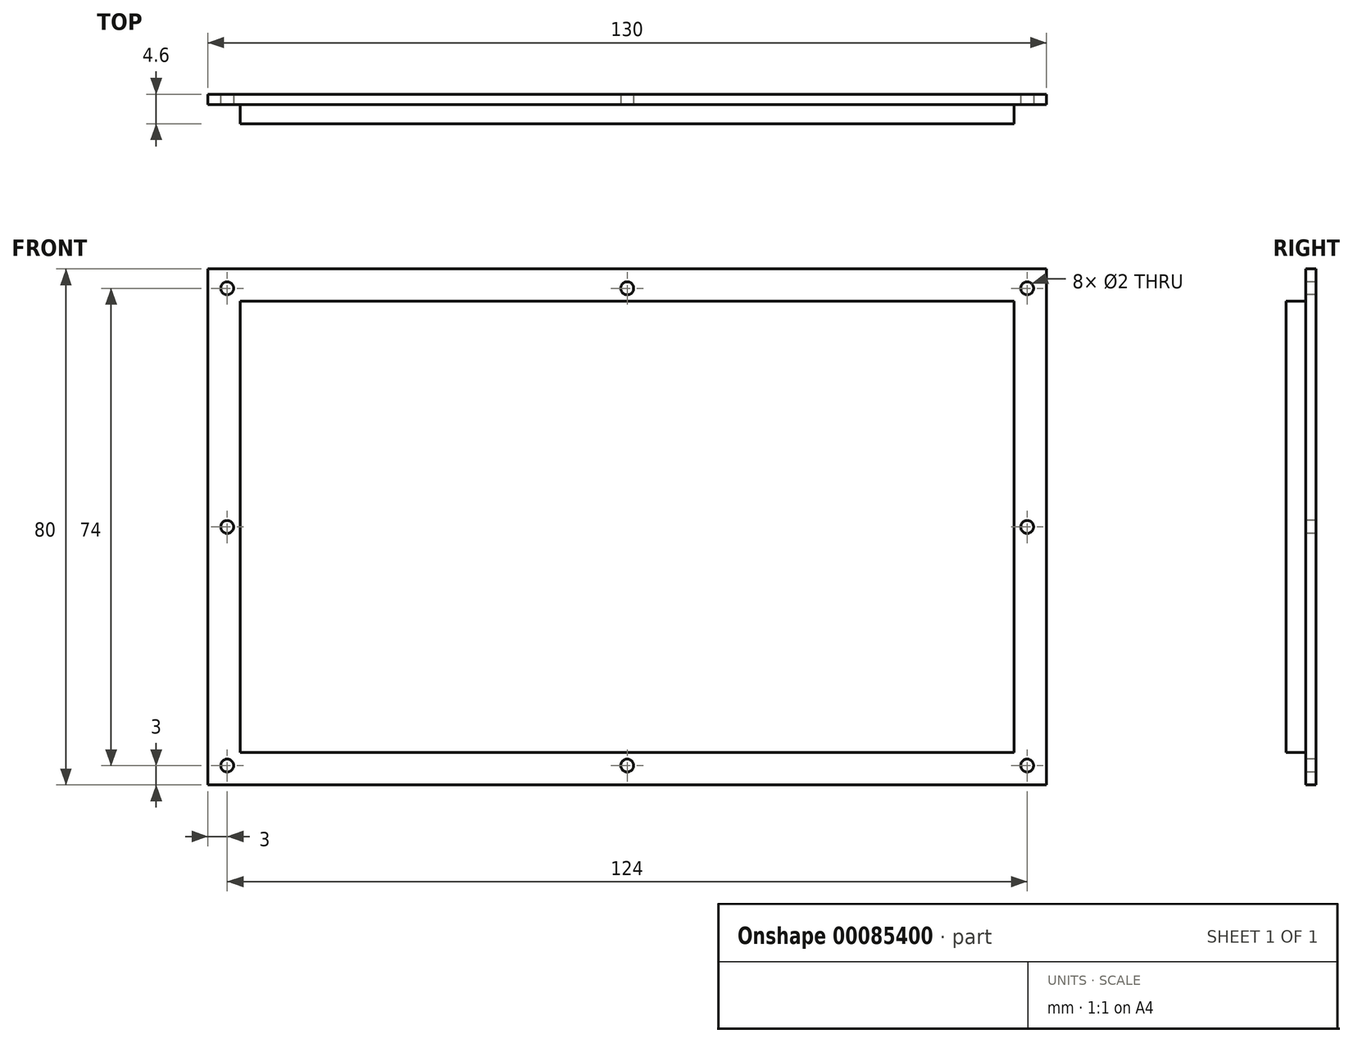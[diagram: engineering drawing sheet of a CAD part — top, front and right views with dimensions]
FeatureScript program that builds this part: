
annotation { "Feature Type Name" : "Feature", "Feature Type Description" : "" }
export const myFeature = defineFeature(function(context is Context, id is Id, definition is map)
    precondition{}
    {
        {
            var Q0;
            Q0=qCreatedBy(makeId("Front.planeOp"),FACE);
            var sketch = newSketch(context, id + "F0", { "sketchPlane" : qUnion([Q0])});
            skLineSegment(sketch, "E0.rect.bottom", {"start": v(60, -35) * mm, "end": v(-60, -35) * mm});
            skLineSegment(sketch, "E0.rect.top", {"start": v(60, 35) * mm, "end": v(-60, 35) * mm});
            skLineSegment(sketch, "E0.rect.left", {"start": v(60, -35) * mm, "end": v(60, 35) * mm});
            skLineSegment(sketch, "E0.rect.right", {"start": v(-60, -35) * mm, "end": v(-60, 35) * mm});
            skPoint(sketch, "E0.rect.middle", {"position": v(0, 0) * mm});
            skSolve(sketch);
        }
        {
            var Q0;
            Q0=qCreatedBy(makeId("Front.planeOp"),FACE);
            var sketch = newSketch(context, id + "F1", { "sketchPlane" : qUnion([Q0])});
            skLineSegment(sketch, "E1.bottom", {"start": v(65, 40) * mm, "end": v(-65, 40) * mm});
            skLineSegment(sketch, "E1.top", {"start": v(65, -40) * mm, "end": v(-65, -40) * mm});
            skLineSegment(sketch, "E1.left", {"start": v(65, 40) * mm, "end": v(65, -40) * mm});
            skLineSegment(sketch, "E1.right", {"start": v(-65, 40) * mm, "end": v(-65, -40) * mm});
            skPoint(sketch, "E2", {"position": v(62, 37) * mm});
            skPoint(sketch, "E3.MirrorP", {"position": v(62, -37) * mm});
            skPoint(sketch, "E4.MirrorP", {"position": v(-62, 37) * mm});
            skPoint(sketch, "E5.MirrorP", {"position": v(-62, -37) * mm});
            skPoint(sketch, "E6", {"position": v(-62, 0) * mm});
            skPoint(sketch, "E7", {"position": v(0, -37) * mm});
            skPoint(sketch, "E8.MirrorP", {"position": v(0, 37) * mm});
            skPoint(sketch, "E9.MirrorP", {"position": v(62, 0) * mm});
            skSolve(sketch);
        }
        {
            var Q0;
            Q0=makeQuery(id+"F0.imprint","IMPRINT",FACE,{"disambiguationData":[TD([[makeQuery(id+"F0.imprint","IMPRINT",EDGE,{"derivedFrom":sQuery(id+"F0.wireOp",EDGE,"E0.rect.bottom")}),-1.0]])]});
            extrude(context, id + "F2", {"entities" : qUnion([Q0]), "depth" : 3 * mm});
        }
        {
            var Q0;
            Q0=makeQuery(id+"F1.imprint","IMPRINT",FACE,{"disambiguationData":[TD([[makeQuery(id+"F1.imprint","IMPRINT",EDGE,{"derivedFrom":sQuery(id+"F1.wireOp",EDGE,"E1.bottom")}),1.0]])]});
            extrude(context, id + "F3", {"entities" : qUnion([Q0]), "operationType" : NewBodyOperationType.ADD, "oppositeDirection" : true, "depth" : 1.6 * mm});
        }
        {
            var Q0;
            Q0=sQuery(id+"F1.wireOp",VERTEX,"E2");
            var Q1;
            Q1=sQuery(id+"F1.wireOp",VERTEX,"E9.MirrorP");
            var Q2;
            Q2=sQuery(id+"F1.wireOp",VERTEX,"E3.MirrorP");
            var Q3;
            Q3=sQuery(id+"F1.wireOp",VERTEX,"E7");
            var Q4;
            Q4=sQuery(id+"F1.wireOp",VERTEX,"E8.MirrorP");
            var Q5;
            Q5=sQuery(id+"F1.wireOp",VERTEX,"E4.MirrorP");
            var Q6;
            Q6=sQuery(id+"F1.wireOp",VERTEX,"E6");
            var Q7;
            Q7=sQuery(id+"F1.wireOp",VERTEX,"E5.MirrorP");
            var Q8;
            Q8=makeQuery(id+"F2.opExtrude","SWEPT_BODY",BODY,{"disambiguationData":[OSD([sQuery(id+"F0.wireOp",EDGE,"E0.rect.bottom"),sQuery(id+"F0.wireOp",EDGE,"E0.rect.top"),sQuery(id+"F0.wireOp",EDGE,"E0.rect.left"),sQuery(id+"F0.wireOp",EDGE,"E0.rect.right")])]});
            hole(context, id + "F4", {"style" : HoleStyle.SIMPLE, "endStyle" : HoleEndStyle.THROUGH, "holeDiameter" : 2 * mm, "locations" : qUnion([Q0, Q1, Q2, Q3, Q4, Q5, Q6, Q7]), "scope" : qUnion([Q8]), "isTappedThrough" : true});
        }
    });
